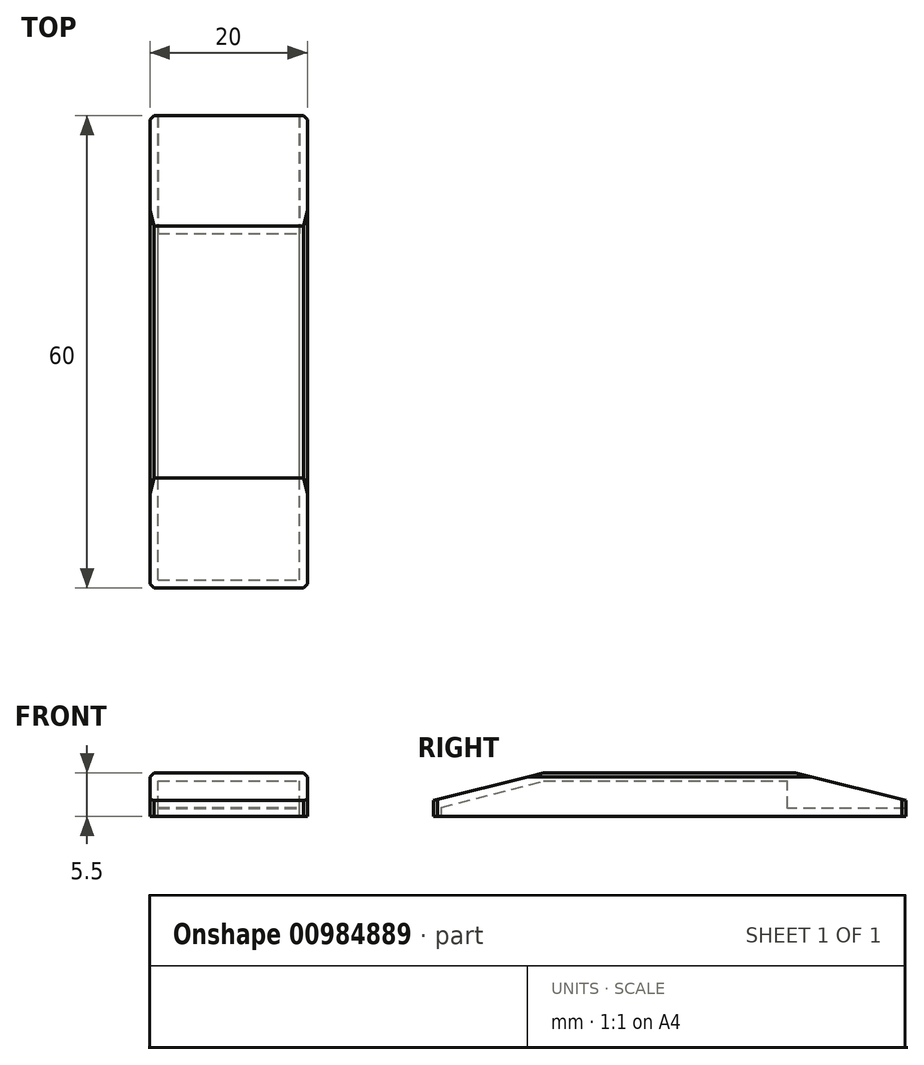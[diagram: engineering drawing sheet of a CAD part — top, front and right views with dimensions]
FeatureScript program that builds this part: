
annotation { "Feature Type Name" : "Feature", "Feature Type Description" : "" }
export const myFeature = defineFeature(function(context is Context, id is Id, definition is map)
    precondition{}
    {
        {
            var Q0;
            Q0=qCreatedBy(makeId("Top.planeOp"),FACE);
            var sketch = newSketch(context, id + "F0", { "sketchPlane" : qUnion([Q0])});
            skLineSegment(sketch, "E0.bottom", {"start": v(10, 30) * mm, "end": v(-10, 30) * mm});
            skLineSegment(sketch, "E0.top", {"start": v(10, -30) * mm, "end": v(-10, -30) * mm});
            skLineSegment(sketch, "E0.left", {"start": v(10, 30) * mm, "end": v(10, -30) * mm});
            skLineSegment(sketch, "E0.right", {"start": v(-10, 30) * mm, "end": v(-10, -30) * mm});
            skPoint(sketch, "E0.middle", {"position": v(0, 0) * mm});
            skSolve(sketch);
        }
        {
            var Q0;
            Q0=makeQuery(id+"F0.imprint","IMPRINT",FACE,{"disambiguationData":[TD([[makeQuery(id+"F0.imprint","IMPRINT",EDGE,{"derivedFrom":sQuery(id+"F0.wireOp",EDGE,"E0.bottom")}),1.0]])]});
            extrude(context, id + "F1", {"entities" : qUnion([Q0]), "depth" : 5.5 * mm, "offsetDistance" : 25 * mm});
        }
        {
            var Q0;
            Q0=qCreatedBy(makeId("Right.planeOp"),FACE);
            var sketch = newSketch(context, id + "F2", { "sketchPlane" : qUnion([Q0])});
            skLineSegment(sketch, "E1.top", {"start": v(-16, 4.5) * mm, "end": v(15, 4.5) * mm});
            skLineSegment(sketch, "E1.right", {"start": v(15, 1) * mm, "end": v(15, 4.5) * mm});
            skLineSegment(sketch, "E2", {"start": v(-29, 0) * mm, "end": v(-29, 1.1) * mm});
            skLineSegment(sketch, "E3", {"start": v(-29, 1.1) * mm, "end": v(-16, 4.5) * mm});
            skLineSegment(sketch, "E4", {"start": v(-29, 0) * mm, "end": v(30, 0) * mm});
            skLineSegment(sketch, "E5", {"start": v(30, 0) * mm, "end": v(30, 1) * mm});
            skLineSegment(sketch, "E6", {"start": v(30, 1) * mm, "end": v(15, 1) * mm});
            skSolve(sketch);
        }
        {
            var Q0;
            Q0 = qSketchRegion(id + "F2", true);
            extrude(context, id + "F3", {"entities" : qUnion([Q0]), "operationType" : NewBodyOperationType.REMOVE, "endBound" : BoundingType.SYMMETRIC, "oppositeDirection" : true, "depth" : 18 * mm, "offsetDistance" : 25 * mm});
        }
        {
            var Q0;
            Q0=makeQuery(id+"F1.opExtrude","SWEPT_FACE",FACE,{"disambiguationData":[OSD([sQuery(id+"F0.wireOp",EDGE,"E0.left")])]});
            var sketch = newSketch(context, id + "F4", { "sketchPlane" : qUnion([Q0])});
            skLineSegment(sketch, "E7", {"start": v(-30, 2) * mm, "end": v(-30, 5.5) * mm});
            skLineSegment(sketch, "E8", {"start": v(-30, 5.5) * mm, "end": v(-16, 5.5) * mm});
            skLineSegment(sketch, "E9", {"start": v(-16, 5.5) * mm, "end": v(-30, 2) * mm});
            skLineSegment(sketch, "E10", {"start": v(30, 2) * mm, "end": v(30, 5.5) * mm});
            skLineSegment(sketch, "E11", {"start": v(30, 5.5) * mm, "end": v(16, 5.5) * mm});
            skLineSegment(sketch, "E12", {"start": v(16, 5.5) * mm, "end": v(30, 2) * mm});
            skSolve(sketch);
        }
        {
            var Q0;
            Q0 = qSketchRegion(id + "F4", true);
            var Q1;
            Q1=makeQuery(id+"F1.opExtrude","SWEPT_FACE",FACE,{"disambiguationData":[OSD([sQuery(id+"F0.wireOp",EDGE,"E0.right")])]});
            extrude(context, id + "F5", {"entities" : qUnion([Q0]), "operationType" : NewBodyOperationType.REMOVE, "endBound" : BoundingType.UP_TO_SURFACE, "oppositeDirection" : true, "depth" : 25 * mm, "endBoundEntityFace" : qUnion([Q1]), "offsetDistance" : 25 * mm});
        }
        {
            var Q0;
            Q0=makeQuery(id+"F5.boolean.opBoolean","COPY",EDGE,{"derivedFrom":makeQuery(id+"F5.opExtrude","CAP_EDGE",EDGE,{"disambiguationData":[OSD([sQuery(id+"F4.wireOp",EDGE,"E12")])],"isStart":false})});
            var Q1;
            Q1=makeQuery(id+"F1.opExtrude","CAP_EDGE",EDGE,{"disambiguationData":[OSD([sQuery(id+"F0.wireOp",EDGE,"E0.right")])],"isStart":false});
            var Q2;
            Q2=makeQuery(id+"F5.boolean.opBoolean","COPY",EDGE,{"derivedFrom":makeQuery(id+"F5.opExtrude","CAP_EDGE",EDGE,{"disambiguationData":[OSD([sQuery(id+"F4.wireOp",EDGE,"E9")])],"isStart":false})});
            var Q3;
            Q3=makeQuery(id+"F1.opExtrude","SWEPT_EDGE",EDGE,{"disambiguationData":[OSD([sQuery(id+"F0.wireOp",EDGE,"E0.top"),sQuery(id+"F0.wireOp",EDGE,"E0.right")])]});
            var Q4;
            Q4=makeQuery(id+"F5.boolean.opBoolean","COPY",EDGE,{"derivedFrom":makeQuery(id+"F5.opExtrude","SWEPT_EDGE",EDGE,{"disambiguationData":[OSD([sQuery(id+"F0.wireOp",EDGE,"E0.top"),sQuery(id+"F0.wireOp",EDGE,"E0.left"),sQuery(id+"F4.wireOp",EDGE,"E7"),sQuery(id+"F4.wireOp",EDGE,"E9")])]})});
            var Q5;
            Q5=makeQuery(id+"F5.boolean.opBoolean","COPY",EDGE,{"derivedFrom":makeQuery(id+"F5.opExtrude","SWEPT_EDGE",EDGE,{"disambiguationData":[OSD([sQuery(id+"F0.wireOp",EDGE,"E0.left"),sQuery(id+"F4.wireOp",EDGE,"E8"),sQuery(id+"F4.wireOp",EDGE,"E9")])]})});
            var Q6;
            Q6=makeQuery(id+"F1.opExtrude","SWEPT_EDGE",EDGE,{"disambiguationData":[OSD([sQuery(id+"F0.wireOp",EDGE,"E0.top"),sQuery(id+"F0.wireOp",EDGE,"E0.left")])]});
            var Q7;
            Q7=makeQuery(id+"F5.boolean.opBoolean","COPY",EDGE,{"derivedFrom":makeQuery(id+"F5.opExtrude","CAP_EDGE",EDGE,{"disambiguationData":[OSD([sQuery(id+"F4.wireOp",EDGE,"E9")])],"isStart":true})});
            var Q8;
            Q8=makeQuery(id+"F1.opExtrude","CAP_EDGE",EDGE,{"disambiguationData":[OSD([sQuery(id+"F0.wireOp",EDGE,"E0.left")])],"isStart":false});
            var Q9;
            Q9=makeQuery(id+"F5.boolean.opBoolean","COPY",EDGE,{"derivedFrom":makeQuery(id+"F5.opExtrude","CAP_EDGE",EDGE,{"disambiguationData":[OSD([sQuery(id+"F4.wireOp",EDGE,"E12")])],"isStart":true})});
            var Q10;
            Q10=makeQuery(id+"F5.boolean.opBoolean","COPY",EDGE,{"derivedFrom":makeQuery(id+"F5.opExtrude","SWEPT_EDGE",EDGE,{"disambiguationData":[OSD([sQuery(id+"F0.wireOp",EDGE,"E0.left"),sQuery(id+"F4.wireOp",EDGE,"E11"),sQuery(id+"F4.wireOp",EDGE,"E12")])]})});
            var Q11;
            Q11=makeQuery(id+"F1.opExtrude","SWEPT_EDGE",EDGE,{"disambiguationData":[OSD([sQuery(id+"F0.wireOp",EDGE,"E0.bottom"),sQuery(id+"F0.wireOp",EDGE,"E0.right")])]});
            var Q12;
            Q12=makeQuery(id+"F5.boolean.opBoolean","COPY",EDGE,{"derivedFrom":makeQuery(id+"F5.opExtrude","SWEPT_EDGE",EDGE,{"disambiguationData":[OSD([sQuery(id+"F0.wireOp",EDGE,"E0.bottom"),sQuery(id+"F0.wireOp",EDGE,"E0.left"),sQuery(id+"F4.wireOp",EDGE,"E10"),sQuery(id+"F4.wireOp",EDGE,"E12")])]})});
            var Q13;
            Q13=makeQuery(id+"F1.opExtrude","SWEPT_EDGE",EDGE,{"disambiguationData":[OSD([sQuery(id+"F0.wireOp",EDGE,"E0.bottom"),sQuery(id+"F0.wireOp",EDGE,"E0.left")])]});
            chamfer(context, id + "F6", {"entities" : qUnion([Q0, Q1, Q2, Q3, Q4, Q5, Q6, Q7, Q8, Q9, Q10, Q11, Q12, Q13]), "width" : 0.5 * mm, "tangentPropagation" : true});
        }
    });
